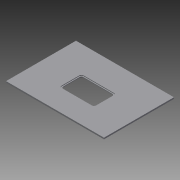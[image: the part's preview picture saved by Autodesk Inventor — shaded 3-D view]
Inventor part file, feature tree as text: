
AUTODESK INVENTOR PART (.ipt)
format: ipt  version: 2015 SP1 (Build 190203100, 203)  size: 128,000 bytes
history: native  units: mm
features: extrude x4, sketch x4, projected_geometry x2, fillet x1
ambient origin geometry x8: Origin, YZ Plane, XZ Plane, XY Plane, X Axis, Y Axis, Z Axis, Center Point
bodies: Solid1 (feature_tree)
feature tree (11):
  extrude  "Extrusion1"  Depth=400.0mm
  extrude  "Extrusion2"  Depth=126.0mm
  fillet  "Fillet1"  Radius=181.25mm
  extrude  "Extrusion3"  Depth=5.0mm
  extrude  "Extrusion4"  Depth=5.0mm
  sketch  "Sketch1"  dims[d0=560.0mm d1=400.0mm]
  sketch  "Sketch2"  dims[d2=8.0mm d3=0.0mm d5=126.0mm d6=181.25mm]
  sketch  "Sketch3"  dims[d7=150.0mm d8=5.0mm]
  projected_geometry  "Projected Loop1"
  sketch  "Sketch4"  dims[d9=5.0mm d10=5.0mm d11=5.0mm d12=4.0mm d13=0.0mm d14=12.0mm d15=4.0mm d16=0.0mm d17=5.0mm d18=5.0mm d19=5.0mm d20=5.0mm d21=12.0mm d22=4.0mm d23=0.0mm]
  projected_geometry  "Projected Loop2"
